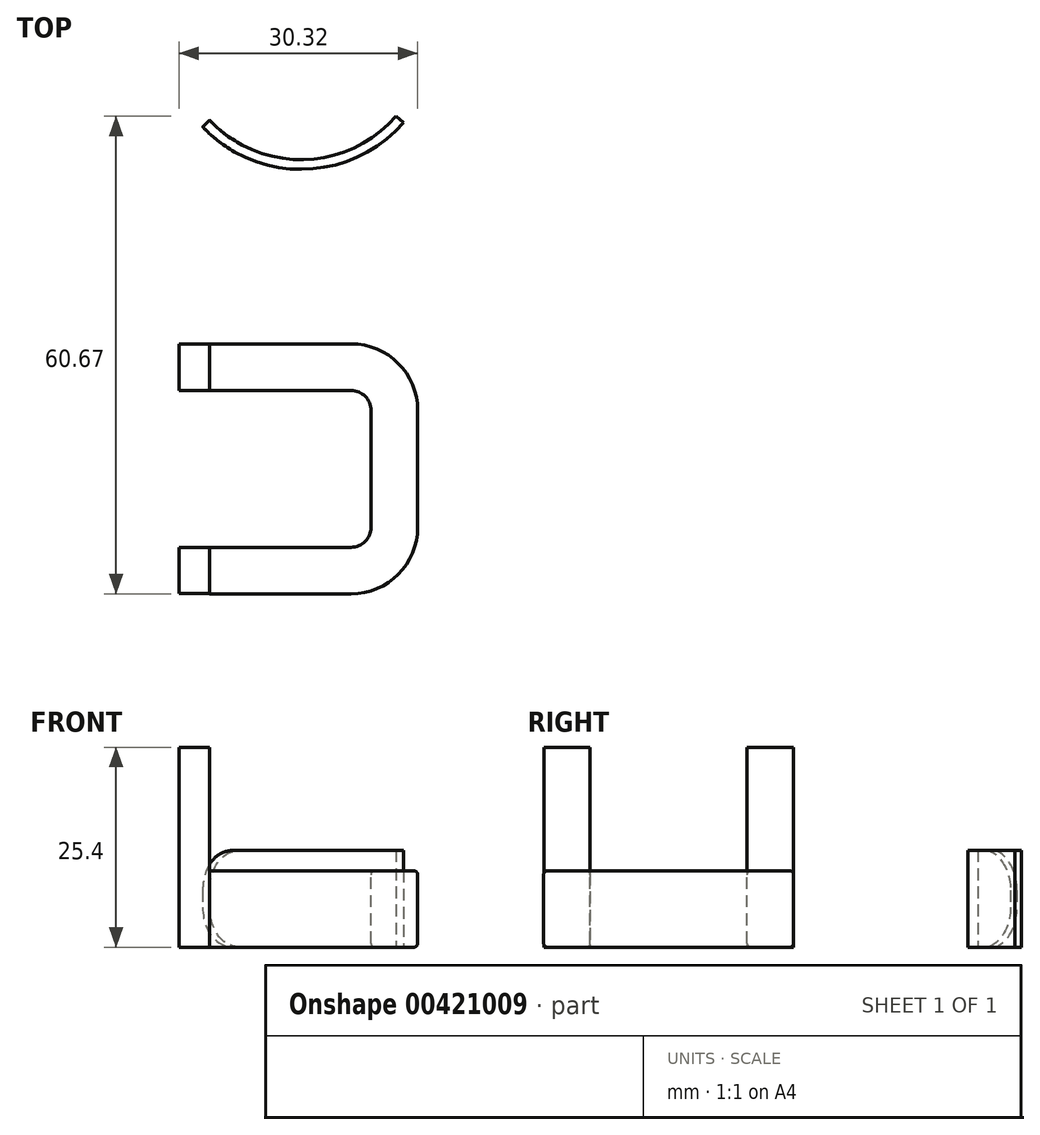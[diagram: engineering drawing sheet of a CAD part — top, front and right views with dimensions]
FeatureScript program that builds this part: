
annotation { "Feature Type Name" : "Feature", "Feature Type Description" : "" }
export const myFeature = defineFeature(function(context is Context, id is Id, definition is map)
    precondition{}
    {
        {
            var Q0;
            Q0=qCreatedBy(makeId("Top.planeOp"),FACE);
            var sketch = newSketch(context, id + "F0", { "sketchPlane" : qUnion([Q0])});
            skLineSegment(sketch, "E0", {"start": v(0, 0) * mm, "end": v(17.96, 0) * mm});
            skLineSegment(sketch, "E1", {"start": v(20.5, -2.54) * mm, "end": v(20.5, -17.38) * mm});
            skLineSegment(sketch, "E2", {"start": v(17.96, -19.92) * mm, "end": v(0, -19.92) * mm});
            skPoint(sketch, "E3.visualSharp", {"position": v(20.5, 0) * mm});
            skArc(sketch, "E3.filletArc", {"start": v(20.5, -2.54) * mm, "mid": v(19.75, -0.74) * mm, "end": v(17.96, 0) * mm});
            skPoint(sketch, "E4.visualSharp", {"position": v(0, 0) * mm});
            skPoint(sketch, "E5.visualSharp", {"position": v(20.5, -19.92) * mm});
            skArc(sketch, "E5.filletArc", {"start": v(17.96, -19.92) * mm, "mid": v(19.75, -19.18) * mm, "end": v(20.5, -17.38) * mm});
            skSolve(sketch);
        }
        {
            var Q0;
            Q0=qCreatedBy(makeId("Right.planeOp"),FACE);
            var sketch = newSketch(context, id + "F1", { "sketchPlane" : qUnion([Q0])});
            skLineSegment(sketch, "E6.bottom", {"start": v(0.5, 0) * mm, "end": v(5.4, 0) * mm});
            skLineSegment(sketch, "E6.top", {"start": v(0.5, 9.73) * mm, "end": v(5.4, 9.73) * mm});
            skLineSegment(sketch, "E6.left", {"start": v(0, 0.5) * mm, "end": v(0, 9.22) * mm});
            skLineSegment(sketch, "E6.right", {"start": v(5.92, 0.5) * mm, "end": v(5.92, 9.22) * mm});
            skPoint(sketch, "E7.visualSharp", {"position": v(5.92, 9.73) * mm});
            skArc(sketch, "E7.filletArc", {"start": v(5.92, 9.22) * mm, "mid": v(5.77, 9.58) * mm, "end": v(5.4, 9.73) * mm});
            skPoint(sketch, "E8.visualSharp", {"position": v(0, 9.73) * mm});
            skArc(sketch, "E8.filletArc", {"start": v(0.5, 9.73) * mm, "mid": v(0.15, 9.58) * mm, "end": v(0, 9.22) * mm});
            skPoint(sketch, "E9.visualSharp", {"position": v(0, 0) * mm});
            skArc(sketch, "E9.filletArc", {"start": v(0, 0.5) * mm, "mid": v(0.15, 0.15) * mm, "end": v(0.5, 0) * mm});
            skPoint(sketch, "E10.visualSharp", {"position": v(5.92, 0) * mm});
            skArc(sketch, "E10.filletArc", {"start": v(5.4, 0) * mm, "mid": v(5.77, 0.15) * mm, "end": v(5.92, 0.5) * mm});
            skSolve(sketch);
        }
        {
            var Q0;
            Q0=makeQuery(id+"F1.imprint","IMPRINT",FACE,{"disambiguationData":[TD([[makeQuery(id+"F1.imprint","IMPRINT",EDGE,{"derivedFrom":sQuery(id+"F1.wireOp",EDGE,"E6.bottom")}),1.0]])]});
            var Q1;
            Q1=sQuery(id+"F0.wireOp",EDGE,"E3.filletArc");
            var Q2;
            Q2=sQuery(id+"F0.wireOp",EDGE,"E1");
            var Q3;
            Q3=sQuery(id+"F0.wireOp",EDGE,"E0");
            var Q4;
            Q4=sQuery(id+"F0.wireOp",EDGE,"E5.filletArc");
            var Q5;
            Q5=sQuery(id+"F0.wireOp",EDGE,"E2");
            sweep(context, id + "F2", {"profiles" : qUnion([Q0]), "path" : qUnion([Q1, Q2, Q3, Q4, Q5])});
        }
        {
            var Q0;
            Q0=qCreatedBy(makeId("Top.planeOp"),FACE);
            var sketch = newSketch(context, id + "F3", { "sketchPlane" : qUnion([Q0])});
            skArc(sketch, "E11", {"start": v(0, 34.31) * mm, "mid": v(11.96, 29.32) * mm, "end": v(23.69, 34.83) * mm});
            skArc(sketch, "E12.0", {"start": v(-0.9, 33.47) * mm, "mid": v(11.99, 28.1) * mm, "end": v(24.62, 34.03) * mm});
            skLineSegment(sketch, "E13", {"start": v(23.69, 34.83) * mm, "end": v(24.62, 34.03) * mm});
            skLineSegment(sketch, "E14", {"start": v(0, 34.31) * mm, "end": v(-0.9, 33.47) * mm});
            skSolve(sketch);
        }
        {
            var Q0;
            Q0 = qSketchRegion(id + "F3", true);
            extrude(context, id + "F4", {"entities" : qUnion([Q0]), "depth" : 12.32 * mm});
        }
        {
            var Q0;
            Q0=makeQuery(id+"F4.opExtrude","CAP_EDGE",EDGE,{"disambiguationData":[OSD([sQuery(id+"F3.wireOp",EDGE,"E14")])],"isStart":false});
            fillet(context, id + "F5", {"entities" : qUnion([Q0]), "radius" : 5.08 * mm, "tangentPropagation" : true, "allowEdgeOverflow" : false});
        }
        {
            var Q0;
            Q0=makeQuery(id+"F4.opExtrude","CAP_EDGE",EDGE,{"disambiguationData":[OSD([sQuery(id+"F3.wireOp",EDGE,"E14")])],"isStart":true});
            fillet(context, id + "F6", {"entities" : qUnion([Q0]), "radius" : 5.08 * mm, "tangentPropagation" : true, "allowEdgeOverflow" : false});
        }
        {
            var Q0;
            Q0=qCreatedBy(makeId("Top.planeOp"),FACE);
            var sketch = newSketch(context, id + "F7", { "sketchPlane" : qUnion([Q0])});
            skLineSegment(sketch, "E15.bottom", {"start": v(0, 5.9) * mm, "end": v(-3.9, 5.9) * mm});
            skLineSegment(sketch, "E15.top", {"start": v(0, 0) * mm, "end": v(-3.9, 0) * mm});
            skLineSegment(sketch, "E15.left", {"start": v(0, 5.9) * mm, "end": v(0, 0) * mm});
            skLineSegment(sketch, "E15.right", {"start": v(-3.9, 5.9) * mm, "end": v(-3.9, 0) * mm});
            skLineSegment(sketch, "E16.bottom", {"start": v(0, -19.95) * mm, "end": v(-3.9, -19.95) * mm});
            skLineSegment(sketch, "E16.top", {"start": v(0, -25.8) * mm, "end": v(-3.9, -25.8) * mm});
            skLineSegment(sketch, "E16.left", {"start": v(0, -19.95) * mm, "end": v(0, -25.8) * mm});
            skLineSegment(sketch, "E16.right", {"start": v(-3.9, -19.95) * mm, "end": v(-3.9, -25.8) * mm});
            skSolve(sketch);
        }
        {
            var Q0;
            Q0 = qSketchRegion(id + "F7", true);
            extrude(context, id + "F8", {"entities" : qUnion([Q0]), "operationType" : NewBodyOperationType.ADD, "depth" : 25.4 * mm});
        }
    });
